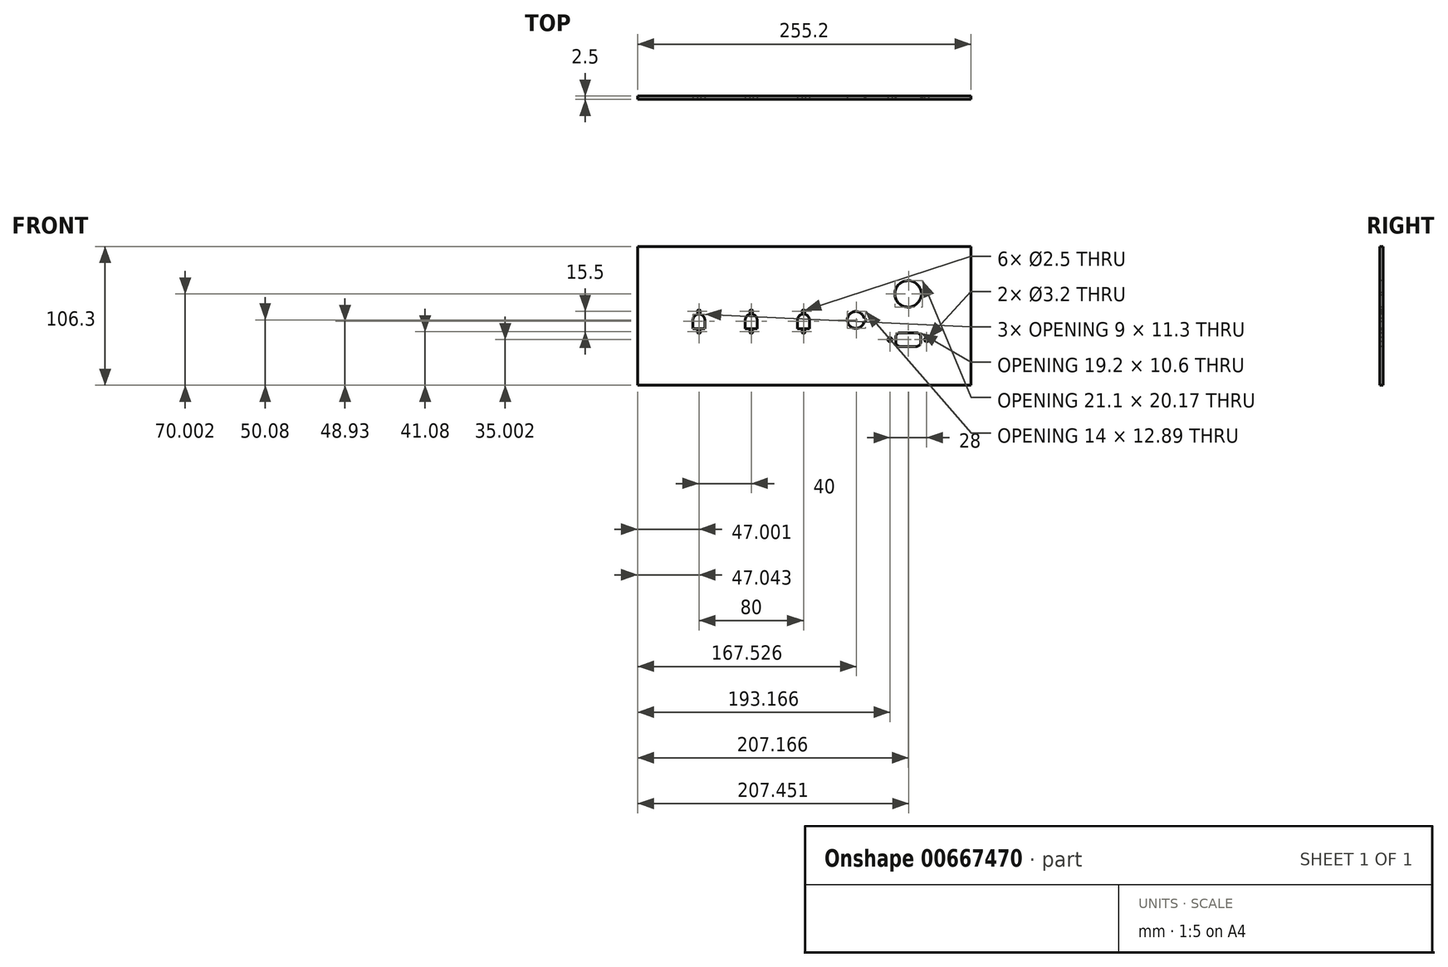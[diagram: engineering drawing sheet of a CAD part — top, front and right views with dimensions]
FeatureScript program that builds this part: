
annotation { "Feature Type Name" : "Feature", "Feature Type Description" : "" }
export const myFeature = defineFeature(function(context is Context, id is Id, definition is map)
    precondition{}
    {
        {
            var Q0;
            Q0=qCreatedBy(makeId("Front.planeOp"),FACE);
            var sketch = newSketch(context, id + "F0", { "sketchPlane" : qUnion([Q0])});
            skLineSegment(sketch, "E0.bottom", {"start": v(119.72, -50.08) * mm, "end": v(-135.48, -50.08) * mm});
            skLineSegment(sketch, "E0.top", {"start": v(119.72, 56.22) * mm, "end": v(-135.48, 56.22) * mm});
            skLineSegment(sketch, "E0.left", {"start": v(119.72, -50.08) * mm, "end": v(119.72, 56.22) * mm});
            skLineSegment(sketch, "E0.right", {"start": v(-135.48, -50.08) * mm, "end": v(-135.48, 56.22) * mm});
            skCircle(sketch, "E1", {"center": v(-88.44, 6.5) * mm, "radius": 1.25 * mm});
            skCircle(sketch, "E2", {"center": v(-88.44, -9) * mm, "radius": 1.25 * mm});
            skLineSegment(sketch, "E3.direction1", {"start": v(-88.44, 6.5) * mm, "end": v(-87.19, 6.5) * mm, "construction": true});
            skLineSegment(sketch, "E4.direction1", {"start": v(-88.44, -9) * mm, "end": v(-87.19, -9) * mm, "construction": true});
            skArc(sketch, "E5", {"start": v(-83.98, 0) * mm, "mid": v(-88.48, 4.5) * mm, "end": v(-92.98, 0) * mm});
            skLineSegment(sketch, "E6.top", {"start": v(-83.98, -6.8) * mm, "end": v(-92.98, -6.8) * mm});
            skLineSegment(sketch, "E6.left", {"start": v(-83.98, 0) * mm, "end": v(-83.98, -6.8) * mm});
            skLineSegment(sketch, "E6.right", {"start": v(-92.98, 0) * mm, "end": v(-92.98, -6.8) * mm});
            skPoint(sketch, "E7.direction1.start.orphan", {"position": v(-88.48, 4.5) * mm});
            skPoint(sketch, "E8.1.0.0", {"position": v(-48.48, 4.5) * mm});
            skLineSegment(sketch, "E8.1.0.1", {"start": v(-52.98, 0) * mm, "end": v(-52.98, -6.8) * mm});
            skCircle(sketch, "E8.1.0.2", {"center": v(-48.44, -9) * mm, "radius": 1.25 * mm});
            skCircle(sketch, "E8.1.0.3", {"center": v(-48.44, 6.5) * mm, "radius": 1.25 * mm});
            skLineSegment(sketch, "E8.1.0.4", {"start": v(-43.98, 0) * mm, "end": v(-43.98, -6.8) * mm});
            skArc(sketch, "E8.1.0.5", {"start": v(-43.98, 0) * mm, "mid": v(-48.48, 4.5) * mm, "end": v(-52.98, 0) * mm});
            skLineSegment(sketch, "E8.1.0.6", {"start": v(-43.98, -6.8) * mm, "end": v(-52.98, -6.8) * mm});
            skLineSegment(sketch, "E8.1.0.7", {"start": v(-48.44, 6.5) * mm, "end": v(-47.19, 6.5) * mm, "construction": true});
            skLineSegment(sketch, "E8.1.0.8", {"start": v(-48.44, -9) * mm, "end": v(-47.19, -9) * mm, "construction": true});
            skPoint(sketch, "E8.2.0.0", {"position": v(-8.48, 4.5) * mm});
            skLineSegment(sketch, "E8.2.0.1", {"start": v(-12.98, 0) * mm, "end": v(-12.98, -6.8) * mm});
            skCircle(sketch, "E8.2.0.2", {"center": v(-8.44, -9) * mm, "radius": 1.25 * mm});
            skCircle(sketch, "E8.2.0.3", {"center": v(-8.44, 6.5) * mm, "radius": 1.25 * mm});
            skLineSegment(sketch, "E8.2.0.4", {"start": v(-3.98, 0) * mm, "end": v(-3.98, -6.8) * mm});
            skArc(sketch, "E8.2.0.5", {"start": v(-3.98, 0) * mm, "mid": v(-8.48, 4.5) * mm, "end": v(-12.98, 0) * mm});
            skLineSegment(sketch, "E8.2.0.6", {"start": v(-3.98, -6.8) * mm, "end": v(-12.98, -6.8) * mm});
            skLineSegment(sketch, "E8.2.0.7", {"start": v(-8.44, 6.5) * mm, "end": v(-7.19, 6.5) * mm, "construction": true});
            skLineSegment(sketch, "E8.2.0.8", {"start": v(-8.44, -9) * mm, "end": v(-7.19, -9) * mm, "construction": true});
            skLineSegment(sketch, "E8.direction1", {"start": v(-92.98, -6.8) * mm, "end": v(-52.98, -6.8) * mm, "construction": true});
            skArc(sketch, "E9", {"start": v(37.88, 1.2) * mm, "mid": v(25.05, 0) * mm, "end": v(37.88, -1.2) * mm});
            skLineSegment(sketch, "E10.bottom", {"start": v(37.88, 1.2) * mm, "end": v(39.05, 1.2) * mm});
            skLineSegment(sketch, "E10.top", {"start": v(37.88, -1.2) * mm, "end": v(39.05, -1.2) * mm});
            skLineSegment(sketch, "E10.right", {"start": v(39.05, 1.2) * mm, "end": v(39.05, -1.2) * mm});
            skArc(sketch, "E11", {"start": v(81.56, 21.02) * mm, "mid": v(61.42, 19.92) * mm, "end": v(81.56, 18.82) * mm});
            skLineSegment(sketch, "E12.bottom", {"start": v(81.56, 21.02) * mm, "end": v(82.52, 21.02) * mm});
            skLineSegment(sketch, "E12.top", {"start": v(81.56, 18.82) * mm, "end": v(82.52, 18.82) * mm});
            skLineSegment(sketch, "E12.right", {"start": v(82.52, 21.02) * mm, "end": v(82.52, 18.82) * mm});
            skCircle(sketch, "E13", {"center": v(57.69, -15.08) * mm, "radius": 1.6 * mm});
            skCircle(sketch, "E14", {"center": v(85.69, -15.08) * mm, "radius": 1.6 * mm});
            skLineSegment(sketch, "E15.bottom", {"start": v(77.79, -20.38) * mm, "end": v(65.59, -20.38) * mm});
            skLineSegment(sketch, "E15.top", {"start": v(77.79, -9.78) * mm, "end": v(65.59, -9.78) * mm});
            skLineSegment(sketch, "E15.left", {"start": v(81.29, -16.88) * mm, "end": v(81.29, -13.28) * mm});
            skLineSegment(sketch, "E15.right", {"start": v(62.09, -16.88) * mm, "end": v(62.09, -13.28) * mm});
            skPoint(sketch, "E15.middle", {"position": v(71.69, -15.08) * mm});
            skPoint(sketch, "E16.visualSharp", {"position": v(62.09, -9.78) * mm});
            skArc(sketch, "E16.filletArc", {"start": v(65.59, -9.78) * mm, "mid": v(63.11, -10.8) * mm, "end": v(62.09, -13.28) * mm});
            skPoint(sketch, "E17.visualSharp", {"position": v(81.29, -9.78) * mm});
            skArc(sketch, "E17.filletArc", {"start": v(81.29, -13.28) * mm, "mid": v(80.26, -10.8) * mm, "end": v(77.79, -9.78) * mm});
            skPoint(sketch, "E18.visualSharp", {"position": v(81.29, -20.38) * mm});
            skArc(sketch, "E18.filletArc", {"start": v(77.79, -20.38) * mm, "mid": v(80.26, -19.35) * mm, "end": v(81.29, -16.88) * mm});
            skPoint(sketch, "E19.visualSharp", {"position": v(62.09, -20.38) * mm});
            skArc(sketch, "E19.filletArc", {"start": v(62.09, -16.88) * mm, "mid": v(63.11, -19.35) * mm, "end": v(65.59, -20.38) * mm});
            skSolve(sketch);
        }
        {
            var Q0;
            Q0=makeQuery(id+"F0.imprint","IMPRINT",FACE,{"disambiguationData":[TD([[makeQuery(id+"F0.imprint","IMPRINT",EDGE,{"derivedFrom":sQuery(id+"F0.wireOp",EDGE,"E0.bottom")}),-1.0]])]});
            extrude(context, id + "F1", {"entities" : qUnion([Q0]), "oppositeDirection" : true, "depth" : 2.5 * mm, "offsetDistance" : 25 * mm});
        }
    });
